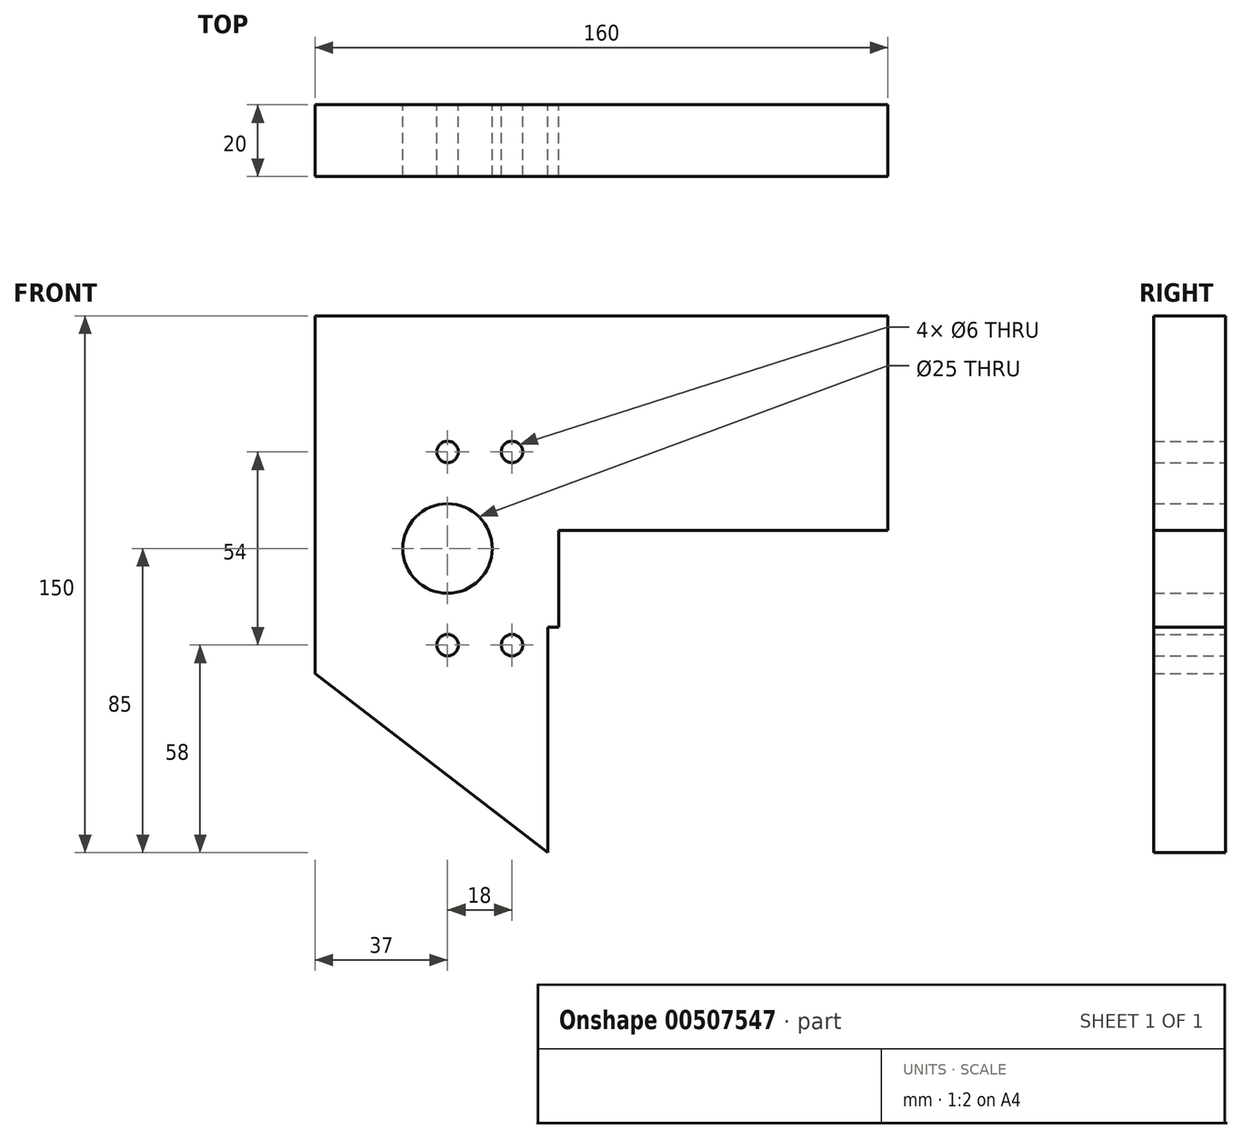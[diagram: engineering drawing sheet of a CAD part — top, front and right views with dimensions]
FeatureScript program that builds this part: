
annotation { "Feature Type Name" : "Feature", "Feature Type Description" : "" }
export const myFeature = defineFeature(function(context is Context, id is Id, definition is map)
    precondition{}
    {
        {
            var Q0;
            Q0=qCreatedBy(makeId("Front.planeOp"),FACE);
            var sketch = newSketch(context, id + "F0", { "sketchPlane" : qUnion([Q0])});
            skLineSegment(sketch, "E0.bottom", {"start": v(60, 0) * mm, "end": v(155, 0) * mm});
            skLineSegment(sketch, "E0.top", {"start": v(-5, 150) * mm, "end": v(155, 150) * mm});
            skLineSegment(sketch, "E0.left", {"start": v(-5, 50) * mm, "end": v(-5, 150) * mm});
            skLineSegment(sketch, "E0.right", {"start": v(155, 0) * mm, "end": v(155, 150) * mm});
            skLineSegment(sketch, "E1.bottom", {"start": v(155, 0) * mm, "end": v(60, 0) * mm});
            skLineSegment(sketch, "E1.top", {"start": v(155, 90) * mm, "end": v(60, 90) * mm});
            skLineSegment(sketch, "E1.left", {"start": v(155, 0) * mm, "end": v(155, 90) * mm});
            skLineSegment(sketch, "E1.right", {"start": v(60, 0) * mm, "end": v(60, 90) * mm});
            skLineSegment(sketch, "E2.bottom", {"start": v(60, 50) * mm, "end": v(-5, 50) * mm});
            skLineSegment(sketch, "E2.top", {"start": v(60, 120) * mm, "end": v(-5, 120) * mm});
            skLineSegment(sketch, "E2.left", {"start": v(60, 50) * mm, "end": v(60, 120) * mm});
            skLineSegment(sketch, "E2.right", {"start": v(-5, 50) * mm, "end": v(-5, 120) * mm});
            skCircle(sketch, "E3", {"center": v(32, 85) * mm, "radius": 18 * mm});
            skLineSegment(sketch, "E4.bottom", {"start": v(1, 63) * mm, "end": v(63, 63) * mm});
            skLineSegment(sketch, "E4.top", {"start": v(1, 107) * mm, "end": v(63, 107) * mm});
            skLineSegment(sketch, "E4.left", {"start": v(1, 63) * mm, "end": v(1, 107) * mm});
            skLineSegment(sketch, "E4.right", {"start": v(63, 63) * mm, "end": v(63, 107) * mm});
            skCircle(sketch, "E5", {"center": v(32, 85) * mm, "radius": 12.5 * mm});
            skLineSegment(sketch, "E6", {"start": v(60, 0) * mm, "end": v(-5, 50) * mm});
            skCircle(sketch, "E7", {"center": v(32, 112) * mm, "radius": 3 * mm});
            skPoint(sketch, "E7.centerSnap0", {"position": v(32, 107) * mm});
            skCircle(sketch, "E8", {"center": v(50, 112) * mm, "radius": 3 * mm});
            skCircle(sketch, "E9", {"center": v(32, 58) * mm, "radius": 3 * mm});
            skCircle(sketch, "E10", {"center": v(50, 58) * mm, "radius": 3 * mm});
            skSolve(sketch);
        }
        {
            var Q0;
            Q0=makeQuery(id+"F0.imprint","IMPRINT",FACE,{"disambiguationData":[TD([[makeQuery(id+"F0.imprint","IMPRINT",EDGE,{"derivedFrom":sQuery(id+"F0.wireOp",EDGE,"E1.bottom")}),-1.0]])]});
            var Q1;
            Q1=makeQuery(id+"F0.imprint","IMPRINT",FACE,{"disambiguationData":[TD([[makeQuery(id+"F0.imprint","IMPRINT",EDGE,{"derivedFrom":sQuery(id+"F0.wireOp",EDGE,"E3")}),-1.0]])]});
            var Q2;
            {var subQ1=sQuery(id+"F0.wireOp",EDGE,"E2.bottom");Q2=makeQuery(id+"F0.imprint","IMPRINT",FACE,{"disambiguationData":[TD([[makeQuery(id+"F0.imprint","IMPRINT",EDGE,{"derivedFrom":subQ1}),-1.0]])]});}
            var Q3;
            Q3=makeQuery(id+"F0.imprint","IMPRINT",FACE,{"disambiguationData":[TD([[makeQuery(id+"F0.imprint","IMPRINT",EDGE,{"derivedFrom":sQuery(id+"F0.wireOp",EDGE,"E0.top")}),-1.0]])]});
            var Q4;
            {var subQ0=sQuery(id+"F0.wireOp",EDGE,"E2.left");var subQ1=sQuery(id+"F0.wireOp",EDGE,"E1.top");var subQ2=makeQuery(id+"F0.imprint","INTERSECT",VERTEX,{"derivedFrom":[subQ1,subQ0]});Q4=makeQuery(id+"F0.imprint","IMPRINT",FACE,{"disambiguationData":[TD([[makeQuery(id+"F0.imprint","IMPRINT",EDGE,{"disambiguationData":[TD([[subQ2,1.0]])],"derivedFrom":subQ1}),-1.0]])]});}
            var Q5;
            {var subQ0=sQuery(id+"F0.wireOp",EDGE,"E2.left");var subQ1=sQuery(id+"F0.wireOp",EDGE,"E1.top");var subQ2=makeQuery(id+"F0.imprint","INTERSECT",VERTEX,{"derivedFrom":[subQ1,subQ0]});Q5=makeQuery(id+"F0.imprint","IMPRINT",FACE,{"disambiguationData":[TD([[makeQuery(id+"F0.imprint","IMPRINT",EDGE,{"disambiguationData":[TD([[subQ2,1.0]])],"derivedFrom":subQ1}),1.0]])]});}
            var Q6;
            Q6=makeQuery(id+"F0.imprint","IMPRINT",FACE,{"disambiguationData":[TD([[makeQuery(id+"F0.imprint","IMPRINT",EDGE,{"derivedFrom":sQuery(id+"F0.wireOp",EDGE,"E5")}),1.0]])]});
            var Q7;
            Q7=makeQuery(id+"F0.imprint","IMPRINT",FACE,{"disambiguationData":[TD([[makeQuery(id+"F0.imprint","IMPRINT",EDGE,{"derivedFrom":sQuery(id+"F0.wireOp",EDGE,"E3")}),1.0]])]});
            var Q8;
            Q8=makeQuery(id+"F0.imprint","IMPRINT",FACE,{"disambiguationData":[TD([[makeQuery(id+"F0.imprint","IMPRINT",EDGE,{"derivedFrom":sQuery(id+"F0.wireOp",EDGE,"E1.right")}),1.0]])]});
            extrude(context, id + "F1", {"entities" : qUnion([Q0, Q1, Q2, Q3, Q4, Q5, Q6, Q7, Q8]), "depth" : 20 * mm, "offsetDistance" : 25 * mm});
        }
        {
            var Q0;
            Q0=makeQuery(id+"F0.imprint","IMPRINT",FACE,{"disambiguationData":[TD([[makeQuery(id+"F0.imprint","IMPRINT",EDGE,{"derivedFrom":sQuery(id+"F0.wireOp",EDGE,"E5")}),1.0]])]});
            extrude(context, id + "F2", {"entities" : qUnion([Q0]), "operationType" : NewBodyOperationType.REMOVE, "depth" : 25 * mm, "offsetDistance" : 25 * mm});
        }
        {
            var Q0;
            Q0=makeQuery(id+"F1.opExtrude","CAP_FACE",FACE,{"disambiguationData":[OSD([sQuery(id+"F0.wireOp",EDGE,"E0.top"),sQuery(id+"F0.wireOp",EDGE,"E0.left"),sQuery(id+"F0.wireOp",EDGE,"E0.right"),sQuery(id+"F0.wireOp",EDGE,"E1.bottom"),sQuery(id+"F0.wireOp",EDGE,"E1.left"),sQuery(id+"F0.wireOp",EDGE,"E2.right"),sQuery(id+"F0.wireOp",EDGE,"E6"),sQuery(id+"F0.wireOp",EDGE,"E7"),sQuery(id+"F0.wireOp",EDGE,"E8"),sQuery(id+"F0.wireOp",EDGE,"E9"),sQuery(id+"F0.wireOp",EDGE,"E10")])],"isStart":false});
            var sketch = newSketch(context, id + "F3", { "sketchPlane" : qUnion([Q0])});
            skCircle(sketch, "E11", {"center": v(110, 81.25) * mm, "radius": 3 * mm});
            skCircle(sketch, "E12", {"center": v(146.25, 45) * mm, "radius": 3 * mm});
            skCircle(sketch, "E13", {"center": v(73.75, 45) * mm, "radius": 3 * mm});
            skCircle(sketch, "E14", {"center": v(110, 8.75) * mm, "radius": 3 * mm});
            skSolve(sketch);
        }
        {
            var Q0;
            Q0=qSketchRegion(id+"F3",true);
            extrude(context, id + "F4", {"entities" : qUnion([Q0]), "operationType" : NewBodyOperationType.REMOVE, "oppositeDirection" : true, "depth" : 25 * mm, "offsetDistance" : 25 * mm});
        }
        {
            var Q0;
            Q0=makeQuery(id+"F1.opExtrude","CAP_FACE",FACE,{"disambiguationData":[OSD([sQuery(id+"F0.wireOp",EDGE,"E0.top"),sQuery(id+"F0.wireOp",EDGE,"E0.left"),sQuery(id+"F0.wireOp",EDGE,"E0.right"),sQuery(id+"F0.wireOp",EDGE,"E1.bottom"),sQuery(id+"F0.wireOp",EDGE,"E1.left"),sQuery(id+"F0.wireOp",EDGE,"E2.right"),sQuery(id+"F0.wireOp",EDGE,"E6"),sQuery(id+"F0.wireOp",EDGE,"E7"),sQuery(id+"F0.wireOp",EDGE,"E8"),sQuery(id+"F0.wireOp",EDGE,"E9"),sQuery(id+"F0.wireOp",EDGE,"E10")])],"isStart":true});
            var sketch = newSketch(context, id + "F5", { "sketchPlane" : qUnion([Q0])});
            skCircle(sketch, "E15", {"center": v(-146.25, 45) * mm, "radius": 5.5 * mm});
            skCircle(sketch, "E16", {"center": v(-110, 81.25) * mm, "radius": 5.5 * mm});
            skCircle(sketch, "E17", {"center": v(-73.75, 45) * mm, "radius": 5.5 * mm});
            skCircle(sketch, "E18", {"center": v(-110, 8.75) * mm, "radius": 5.5 * mm});
            skSolve(sketch);
        }
        {
            var Q0;
            Q0 = qSketchRegion(id + "F5", true);
            extrude(context, id + "F6", {"entities" : qUnion([Q0]), "operationType" : NewBodyOperationType.REMOVE, "oppositeDirection" : true, "depth" : 6 * mm, "offsetDistance" : 25 * mm});
        }
    });
